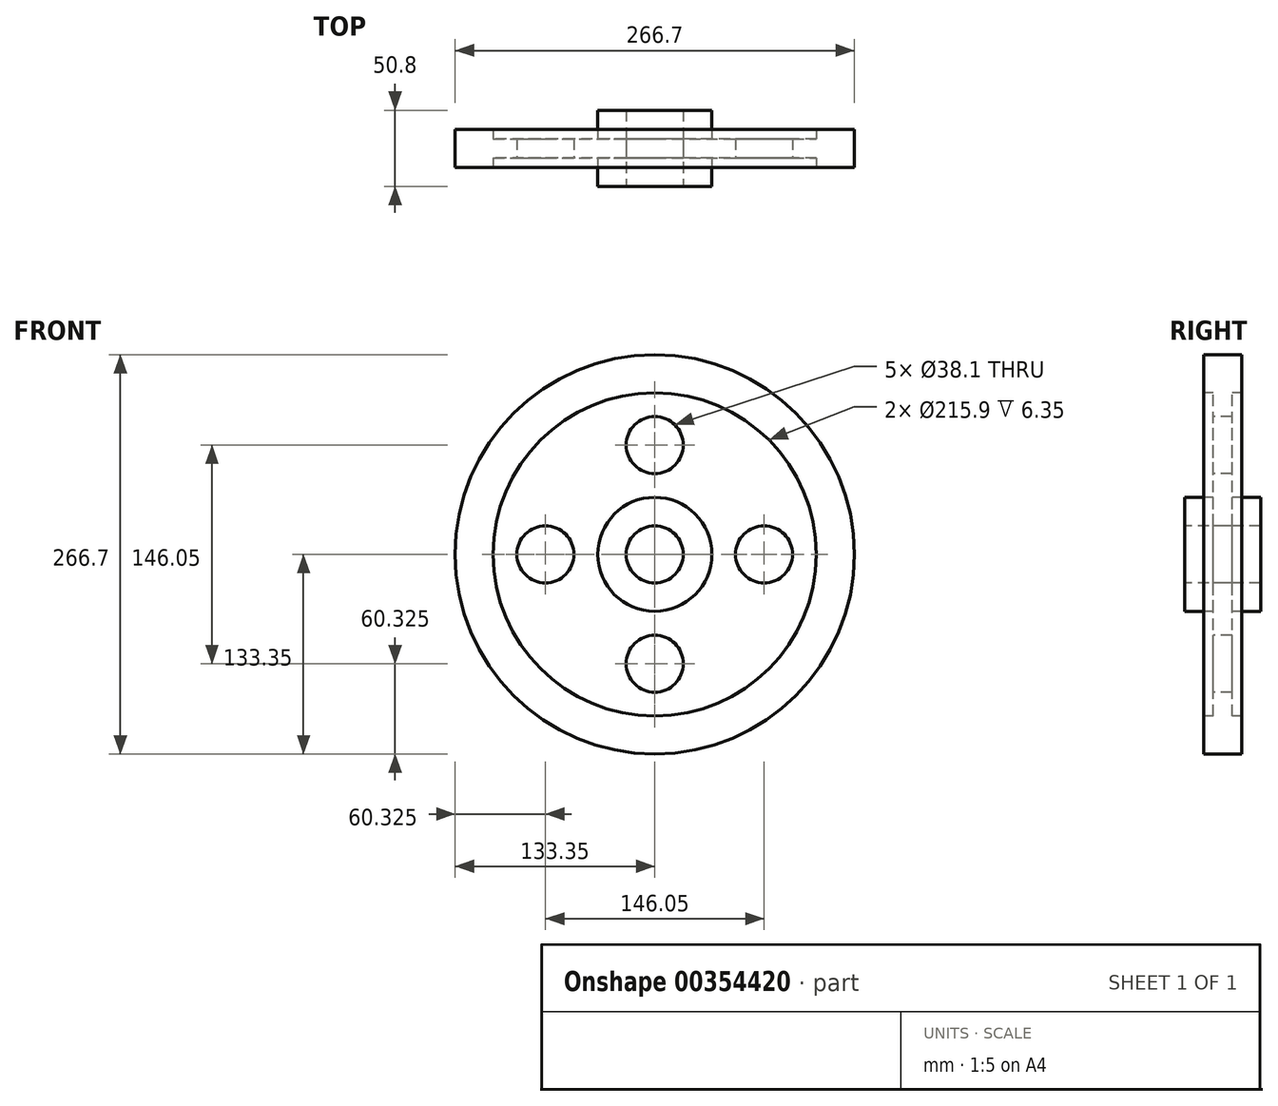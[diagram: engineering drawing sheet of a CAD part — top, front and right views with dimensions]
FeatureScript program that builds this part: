
annotation { "Feature Type Name" : "Feature", "Feature Type Description" : "" }
export const myFeature = defineFeature(function(context is Context, id is Id, definition is map)
    precondition{}
    {
        {
            var Q0;
            Q0=qCreatedBy(makeId("Right.planeOp"),FACE);
            var sketch = newSketch(context, id + "F0", { "sketchPlane" : qUnion([Q0])});
            skLineSegment(sketch, "E0", {"start": v(0, 0) * mm, "end": v(101.6, 0) * mm});
            skLineSegment(sketch, "E1.0", {"start": v(0, 19.05) * mm, "end": v(25.4, 19.05) * mm});
            skLineSegment(sketch, "E2.0", {"start": v(0, 38.1) * mm, "end": v(25.4, 38.1) * mm});
            skLineSegment(sketch, "E3.0", {"start": v(0, 107.95) * mm, "end": v(12.7, 107.95) * mm});
            skLineSegment(sketch, "E4.0", {"start": v(0, 133.35) * mm, "end": v(12.7, 133.35) * mm});
            skLineSegment(sketch, "E5", {"start": v(0, 0) * mm, "end": v(0, 133.35) * mm});
            skLineSegment(sketch, "E6.0", {"start": v(25.4, 19.05) * mm, "end": v(25.4, 38.1) * mm});
            skLineSegment(sketch, "E7.0", {"start": v(12.7, 19.05) * mm, "end": v(12.7, 38.1) * mm});
            skLineSegment(sketch, "E8.0", {"start": v(6.35, 19.05) * mm, "end": v(6.35, 133.35) * mm});
            skLineSegment(sketch, "E9.trimOffspring", {"start": v(12.7, 107.95) * mm, "end": v(12.7, 133.35) * mm});
            skLineSegment(sketch, "E10.MirrorCS", {"start": v(0, 133.35) * mm, "end": v(-12.7, 133.35) * mm});
            skLineSegment(sketch, "E11.MirrorCS", {"start": v(-12.7, 107.95) * mm, "end": v(-12.7, 133.35) * mm});
            skLineSegment(sketch, "E12.MirrorCS", {"start": v(-6.35, 19.05) * mm, "end": v(-6.35, 133.35) * mm});
            skLineSegment(sketch, "E13.MirrorCS", {"start": v(0, 107.95) * mm, "end": v(-12.7, 107.95) * mm});
            skLineSegment(sketch, "E14.MirrorCS", {"start": v(0, 38.1) * mm, "end": v(-25.4, 38.1) * mm});
            skLineSegment(sketch, "E15.MirrorCS", {"start": v(-25.4, 19.05) * mm, "end": v(-25.4, 38.1) * mm});
            skLineSegment(sketch, "E16.MirrorCS", {"start": v(0, 19.05) * mm, "end": v(-25.4, 19.05) * mm});
            skSolve(sketch);
        }
        {
            var Q0;
            {var subQ3=sQuery(id+"F0.wireOp",EDGE,"E10.MirrorCS");var subQ5=sQuery(id+"F0.wireOp",EDGE,"E12.MirrorCS");var subQ6=makeQuery(id+"F0.imprint","INTERSECT",VERTEX,{"derivedFrom":[subQ3,subQ5]});Q0=makeQuery(id+"F0.imprint","IMPRINT",FACE,{"disambiguationData":[TD([[makeQuery(id+"F0.imprint","IMPRINT",EDGE,{"disambiguationData":[TD([[subQ6,1.0]])],"derivedFrom":subQ5}),-1.0]])]});}
            var Q1;
            {var subQ0=sQuery(id+"F0.wireOp",EDGE,"E11.MirrorCS");Q1=makeQuery(id+"F0.imprint","IMPRINT",FACE,{"disambiguationData":[TD([[makeQuery(id+"F0.imprint","IMPRINT",EDGE,{"derivedFrom":subQ0}),-1.0]])]});}
            var Q2;
            {var subQ3=sQuery(id+"F0.wireOp",EDGE,"E8.0");var subQ5=sQuery(id+"F0.wireOp",EDGE,"E4.0");var subQ7=makeQuery(id+"F0.imprint","INTERSECT",VERTEX,{"derivedFrom":[subQ5,subQ3]});Q2=makeQuery(id+"F0.imprint","IMPRINT",FACE,{"disambiguationData":[TD([[makeQuery(id+"F0.imprint","IMPRINT",EDGE,{"disambiguationData":[TD([[subQ7,1.0]])],"derivedFrom":subQ3}),1.0]])]});}
            var Q3;
            {var subQ0=sQuery(id+"F0.wireOp",EDGE,"E9.trimOffspring");Q3=makeQuery(id+"F0.imprint","IMPRINT",FACE,{"disambiguationData":[TD([[makeQuery(id+"F0.imprint","IMPRINT",EDGE,{"derivedFrom":subQ0}),1.0]])]});}
            var Q4;
            {var subQ1=sQuery(id+"F0.wireOp",EDGE,"E2.0");var subQ3=sQuery(id+"F0.wireOp",EDGE,"E8.0");var subQ4=makeQuery(id+"F0.imprint","INTERSECT",VERTEX,{"derivedFrom":[subQ1,subQ3]});Q4=makeQuery(id+"F0.imprint","IMPRINT",FACE,{"disambiguationData":[TD([[makeQuery(id+"F0.imprint","IMPRINT",EDGE,{"disambiguationData":[TD([[subQ4,-1.0]])],"derivedFrom":subQ3}),1.0]])]});}
            var Q5;
            {var subQ0=sQuery(id+"F0.wireOp",EDGE,"E14.MirrorCS");var subQ5=sQuery(id+"F0.wireOp",EDGE,"E12.MirrorCS");var subQ6=makeQuery(id+"F0.imprint","INTERSECT",VERTEX,{"derivedFrom":[subQ5,subQ0]});Q5=makeQuery(id+"F0.imprint","IMPRINT",FACE,{"disambiguationData":[TD([[makeQuery(id+"F0.imprint","IMPRINT",EDGE,{"disambiguationData":[TD([[subQ6,-1.0]])],"derivedFrom":subQ5}),-1.0]])]});}
            var Q6;
            {var subQ0=sQuery(id+"F0.wireOp",EDGE,"E7.0");Q6=makeQuery(id+"F0.imprint","IMPRINT",FACE,{"disambiguationData":[TD([[makeQuery(id+"F0.imprint","IMPRINT",EDGE,{"derivedFrom":subQ0}),1.0]])]});}
            var Q7;
            {var subQ1=sQuery(id+"F0.wireOp",EDGE,"E1.0");var subQ3=sQuery(id+"F0.wireOp",EDGE,"E8.0");var subQ4=makeQuery(id+"F0.imprint","INTERSECT",VERTEX,{"derivedFrom":[subQ1,subQ3]});Q7=makeQuery(id+"F0.imprint","IMPRINT",FACE,{"disambiguationData":[TD([[makeQuery(id+"F0.imprint","IMPRINT",EDGE,{"disambiguationData":[TD([[subQ4,-1.0]])],"derivedFrom":subQ3}),1.0]])]});}
            var Q8;
            {var subQ0=sQuery(id+"F0.wireOp",EDGE,"E16.MirrorCS");var subQ5=sQuery(id+"F0.wireOp",EDGE,"E12.MirrorCS");var subQ6=makeQuery(id+"F0.imprint","INTERSECT",VERTEX,{"derivedFrom":[subQ5,subQ0]});Q8=makeQuery(id+"F0.imprint","IMPRINT",FACE,{"disambiguationData":[TD([[makeQuery(id+"F0.imprint","IMPRINT",EDGE,{"disambiguationData":[TD([[subQ6,-1.0]])],"derivedFrom":subQ5}),-1.0]])]});}
            var Q9;
            {var subQ5=sQuery(id+"F0.wireOp",EDGE,"E15.MirrorCS");Q9=makeQuery(id+"F0.imprint","IMPRINT",FACE,{"disambiguationData":[TD([[makeQuery(id+"F0.imprint","IMPRINT",EDGE,{"derivedFrom":subQ5}),-1.0]])]});}
            var Q10;
            {var subQ0=sQuery(id+"F0.wireOp",EDGE,"E6.0");Q10=makeQuery(id+"F0.imprint","IMPRINT",FACE,{"disambiguationData":[TD([[makeQuery(id+"F0.imprint","IMPRINT",EDGE,{"derivedFrom":subQ0}),1.0]])]});}
            var Q11;
            Q11=sQuery(id+"F0.wireOp",EDGE,"E0");
            revolve(context, id + "F1", {"entities" : qUnion([Q0, Q1, Q2, Q3, Q4, Q5, Q6, Q7, Q8, Q9, Q10]), "axis" : qUnion([Q11]), "revolveType" : RevolveType.FULL});
        }
        {
            var Q0;
            Q0=makeQuery(id+"F1.opRevolve","SWEPT_FACE",FACE,{"disambiguationData":[OSD([sQuery(id+"F0.wireOp",EDGE,"E12.MirrorCS")])]});
            var sketch = newSketch(context, id + "F2", { "sketchPlane" : qUnion([Q0])});
            skLineSegment(sketch, "E17", {"start": v(0, 0) * mm, "end": v(0, 73.03) * mm});
            skCircle(sketch, "E18", {"center": v(0, 73.03) * mm, "radius": 19.05 * mm});
            skCircle(sketch, "E19.1.0", {"center": v(-73.03, 0) * mm, "radius": 19.05 * mm});
            skCircle(sketch, "E19.2.0", {"center": v(0, -73.03) * mm, "radius": 19.05 * mm});
            skCircle(sketch, "E19.3.0", {"center": v(73.03, 0) * mm, "radius": 19.05 * mm});
            skPoint(sketch, "E19.center", {"position": v(0, 0) * mm});
            skSolve(sketch);
        }
        {
            var Q0;
            Q0=makeQuery(id+"F2.imprint","IMPRINT",FACE,{"disambiguationData":[TD([[makeQuery(id+"F2.imprint","IMPRINT",EDGE,{"derivedFrom":sQuery(id+"F2.wireOp",EDGE,"E18")}),1.0]])]});
            var Q1;
            Q1=makeQuery(id+"F2.imprint","IMPRINT",FACE,{"disambiguationData":[TD([[makeQuery(id+"F2.imprint","IMPRINT",EDGE,{"derivedFrom":sQuery(id+"F2.wireOp",EDGE,"E19.3.0")}),1.0]])]});
            var Q2;
            Q2=makeQuery(id+"F2.imprint","IMPRINT",FACE,{"disambiguationData":[TD([[makeQuery(id+"F2.imprint","IMPRINT",EDGE,{"derivedFrom":sQuery(id+"F2.wireOp",EDGE,"E19.2.0")}),1.0]])]});
            var Q3;
            Q3=makeQuery(id+"F2.imprint","IMPRINT",FACE,{"disambiguationData":[TD([[makeQuery(id+"F2.imprint","IMPRINT",EDGE,{"derivedFrom":sQuery(id+"F2.wireOp",EDGE,"E19.1.0")}),1.0]])]});
            extrude(context, id + "F3", {"entities" : qUnion([Q0, Q1, Q2, Q3]), "operationType" : NewBodyOperationType.REMOVE, "oppositeDirection" : true, "depth" : 25.4 * mm});
        }
    });
